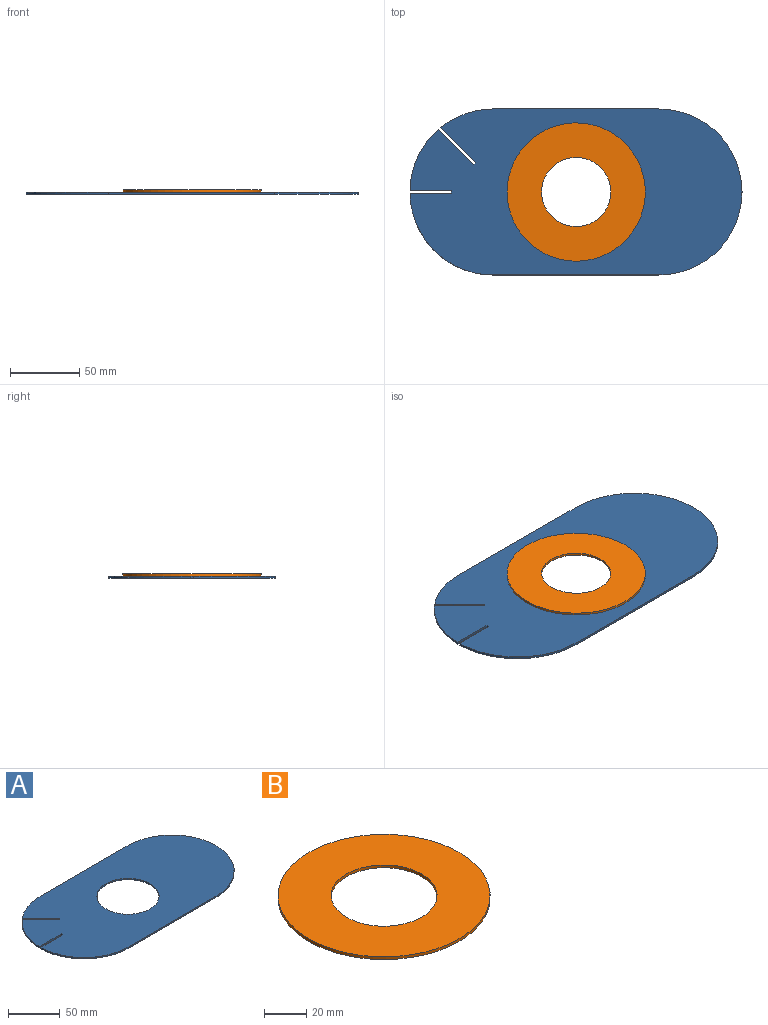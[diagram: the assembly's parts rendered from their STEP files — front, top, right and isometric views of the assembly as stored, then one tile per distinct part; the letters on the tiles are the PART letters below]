
ASSEMBLY  parts=2 mates=1
PART A: 15 faces, bbox 240x120x1.6 mm
  f0: cylinder r=60mm len=59.99mm, axis (0,0,-1), area 148mm2, adj f2,f3,f6,f12
  f1: cylinder r=60mm len=37.96mm, axis (0,0,-1), area 65.2mm2, adj f2,f3,f4,f8
  f2: plane 240.01x120.01mm, normal (0,0,1), area 22750.4mm2, adj f0,f1,f4,f5,f6,f7,f8,f9
  f3: plane 240x120mm, normal (0,0,-1), area 22750.3mm2, adj f0,f1,f4,f5,f6,f7,f8,f9
  f4: plane 120x1.59mm, normal (0,1,0), area 190.5mm2, adj f1,f2,f3,f7
  f5: cylinder r=60mm len=44.17mm, axis (0,0,-1), area 79.6mm2, adj f2,f3,f9,f11
  f6: plane 120x1.59mm, normal (0,-1,0), area 190.5mm2, adj f0,f2,f3,f7
  f7: cylinder r=60mm len=120mm, axis (0,0,-1), area 299.2mm2, adj f2,f3,f4,f6
  f8: plane 25.39x25.39mm, normal (-0.71,-0.71,0), area 57mm2, adj f1,f2,f3,f10
  f9: plane 25.51x25.51mm, normal (0.71,0.71,0), area 57.3mm2, adj f2,f3,f5,f10
  f10: plane 1.59x1.41mm, normal (-0.71,0.71,0), area 3.2mm2, adj f2,f3,f8,f9
  f11: plane 30.02x1.6mm, normal (0,-1,0), area 47.6mm2, adj f2,f3,f5,f13
  f12: plane 30.02x1.6mm, normal (0,1,0), area 47.6mm2, adj f0,f2,f3,f13
  f13: plane 2x1.59mm, normal (-1,0,0), area 3.2mm2, adj f2,f3,f11,f12
  f14: cylinder r=30mm len=60mm, axis (0,0,1), area 299.2mm2, adj f2,f3
PART B: 4 faces, bbox 100x100x1.6 mm
  f0: cylinder r=50mm len=100mm, axis (0,0,-1), area 498.7mm2, adj f1,f2
  f1: plane 100x100mm, normal (0,0,1), area 5890.5mm2, adj f0,f3
  f2: plane 100x100mm, normal (0,0,-1), area 5890.5mm2, adj f0,f3
  f3: cylinder r=25mm len=50mm, axis (0,0,-1), area 249.4mm2, adj f1,f2
PLACE A t=(0.03,-0.33,-0.12)mm
PLACE B t=(-22.21,-0.36,1.47)mm
MATE planar B.f0 <-> A.f2  axis (0,0,-1) through (-22.21,-0.36,1.47)mm
